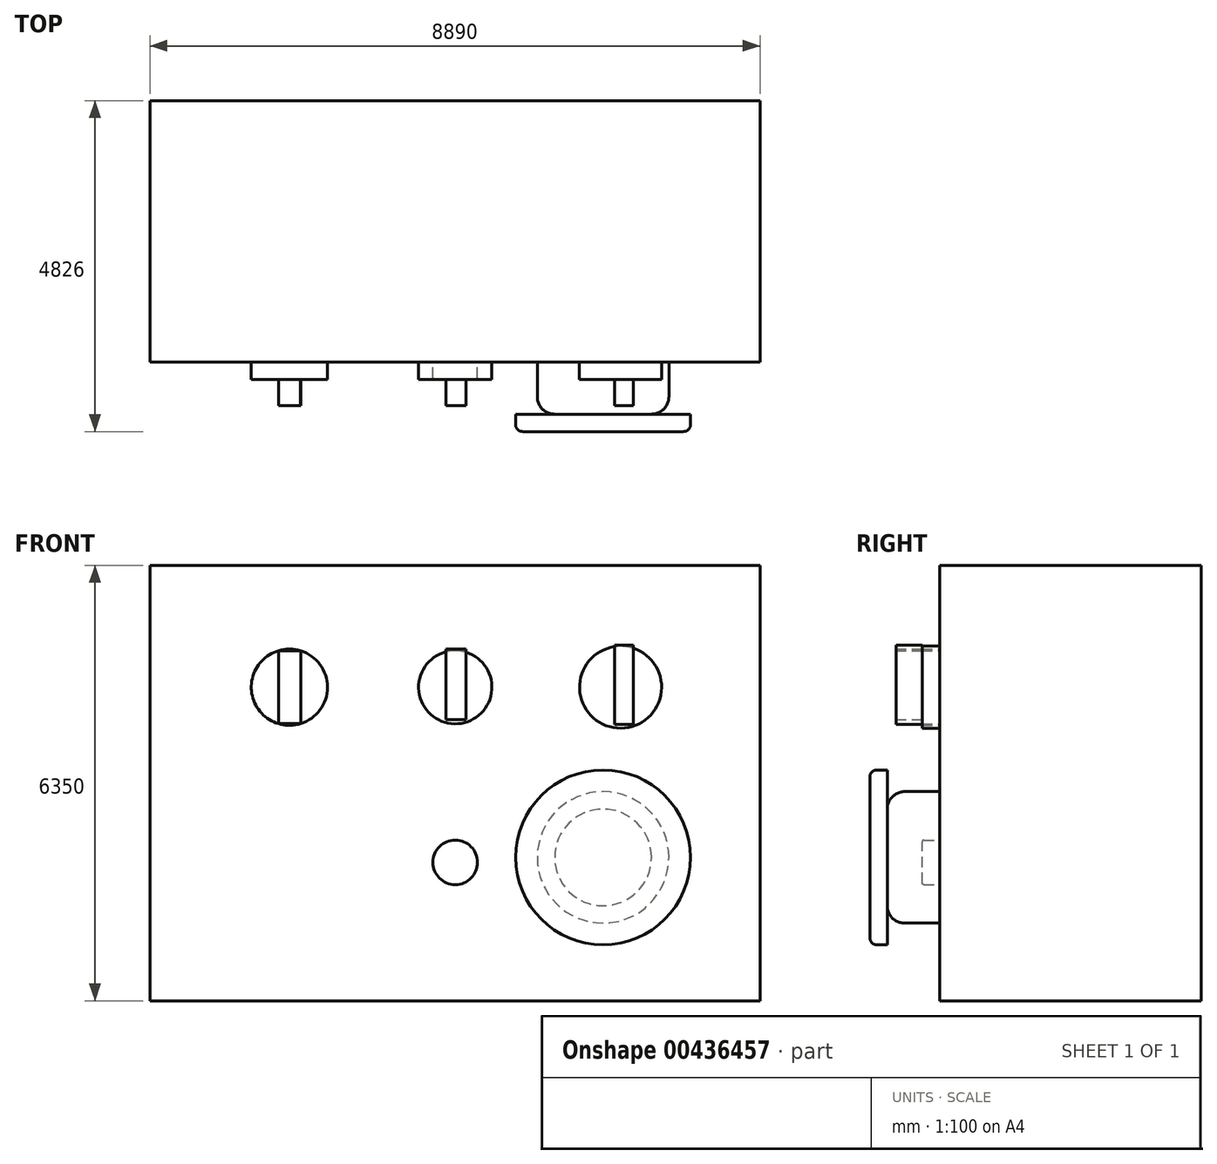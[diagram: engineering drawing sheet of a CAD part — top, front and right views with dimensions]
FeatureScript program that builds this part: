
annotation { "Feature Type Name" : "Feature", "Feature Type Description" : "" }
export const myFeature = defineFeature(function(context is Context, id is Id, definition is map)
    precondition{}
    {
        {
            var Q0;
            Q0=qCreatedBy(makeId("Front.planeOp"),FACE);
            var sketch = newSketch(context, id + "F0", { "sketchPlane" : qUnion([Q0])});
            skLineSegment(sketch, "E0.bottom", {"start": v(-4449.16, 3553.43) * mm, "end": v(4440.84, 3553.43) * mm});
            skLineSegment(sketch, "E0.top", {"start": v(-4449.16, -2796.57) * mm, "end": v(4440.84, -2796.57) * mm});
            skLineSegment(sketch, "E0.left", {"start": v(-4449.16, 3553.43) * mm, "end": v(-4449.16, -2796.57) * mm});
            skLineSegment(sketch, "E0.right", {"start": v(4440.84, 3553.43) * mm, "end": v(4440.84, -2796.57) * mm});
            skSolve(sketch);
        }
        {
            var Q0;
            Q0 = qSketchRegion(id + "F0", true);
            extrude(context, id + "F1", {"entities" : qUnion([Q0]), "depth" : 3810 * mm});
        }
        {
            var Q0;
            Q0=makeQuery(id+"F1.opExtrude","CAP_FACE",FACE,{"disambiguationData":[OSD([sQuery(id+"F0.wireOp",EDGE,"E0.bottom"),sQuery(id+"F0.wireOp",EDGE,"E0.top"),sQuery(id+"F0.wireOp",EDGE,"E0.left"),sQuery(id+"F0.wireOp",EDGE,"E0.right")])],"isStart":false});
            var sketch = newSketch(context, id + "F2", { "sketchPlane" : qUnion([Q0])});
            skCircle(sketch, "E1", {"center": v(-2417.16, 1775.43) * mm, "radius": 554.97 * mm});
            skCircle(sketch, "E2", {"center": v(0, 1775.43) * mm, "radius": 533.86 * mm});
            skCircle(sketch, "E3", {"center": v(2408.84, 1775.43) * mm, "radius": 598.02 * mm});
            skSolve(sketch);
        }
        {
            var Q0;
            Q0=makeQuery(id+"F2.imprint","IMPRINT",FACE,{"disambiguationData":[TD([[makeQuery(id+"F2.imprint","IMPRINT",EDGE,{"derivedFrom":sQuery(id+"F2.wireOp",EDGE,"E1")}),1.0]])]});
            var Q1;
            Q1=makeQuery(id+"F2.imprint","IMPRINT",FACE,{"disambiguationData":[TD([[makeQuery(id+"F2.imprint","IMPRINT",EDGE,{"derivedFrom":sQuery(id+"F2.wireOp",EDGE,"E2")}),1.0]])]});
            var Q2;
            Q2=makeQuery(id+"F2.imprint","IMPRINT",FACE,{"disambiguationData":[TD([[makeQuery(id+"F2.imprint","IMPRINT",EDGE,{"derivedFrom":sQuery(id+"F2.wireOp",EDGE,"E3")}),1.0]])]});
            extrude(context, id + "F3", {"entities" : qUnion([Q0, Q1, Q2]), "operationType" : NewBodyOperationType.ADD, "depth" : 254 * mm});
        }
        {
            var Q0;
            Q0=makeQuery(id+"F3.opExtrude","CAP_FACE",FACE,{"disambiguationData":[OSD([sQuery(id+"F2.wireOp",EDGE,"E1")])],"isStart":false});
            var sketch = newSketch(context, id + "F4", { "sketchPlane" : qUnion([Q0])});
            skLineSegment(sketch, "E4.bottom", {"start": v(-2575.27, 2307.4) * mm, "end": v(-2253, 2307.4) * mm});
            skLineSegment(sketch, "E4.top", {"start": v(-2575.27, 1245.3) * mm, "end": v(-2253, 1245.3) * mm});
            skLineSegment(sketch, "E4.left", {"start": v(-2575.27, 2307.4) * mm, "end": v(-2575.27, 1245.3) * mm});
            skLineSegment(sketch, "E4.right", {"start": v(-2253, 2307.4) * mm, "end": v(-2253, 1245.3) * mm});
            skLineSegment(sketch, "E5.bottom", {"start": v(-135.55, 2328.87) * mm, "end": v(154.96, 2328.87) * mm});
            skLineSegment(sketch, "E5.top", {"start": v(-135.55, 1303.72) * mm, "end": v(154.96, 1303.72) * mm});
            skLineSegment(sketch, "E5.left", {"start": v(-135.55, 2328.87) * mm, "end": v(-135.55, 1303.72) * mm});
            skLineSegment(sketch, "E5.right", {"start": v(154.96, 2328.87) * mm, "end": v(154.96, 1303.72) * mm});
            skLineSegment(sketch, "E6.bottom", {"start": v(2320.28, 2388.38) * mm, "end": v(2593.52, 2388.38) * mm});
            skLineSegment(sketch, "E6.top", {"start": v(2320.28, 1231.47) * mm, "end": v(2593.52, 1231.47) * mm});
            skLineSegment(sketch, "E6.left", {"start": v(2320.28, 2388.38) * mm, "end": v(2320.28, 1231.47) * mm});
            skLineSegment(sketch, "E6.right", {"start": v(2593.52, 2388.38) * mm, "end": v(2593.52, 1231.47) * mm});
            skSolve(sketch);
        }
        {
            var Q0;
            {var subQ1=sQuery(id+"F4.wireOp",EDGE,"E4.top");Q0=makeQuery(id+"F4.imprint","IMPRINT",FACE,{"disambiguationData":[TD([[makeQuery(id+"F4.imprint","IMPRINT",EDGE,{"derivedFrom":subQ1}),1.0]])]});}
            var Q1;
            Q1=makeQuery(id+"F4.imprint","IMPRINT",FACE,{"disambiguationData":[TD([[makeQuery(id+"F4.imprint","IMPRINT",EDGE,{"derivedFrom":sQuery(id+"F4.wireOp",EDGE,"E5.bottom")}),-1.0]])]});
            var Q2;
            Q2=makeQuery(id+"F4.imprint","IMPRINT",FACE,{"disambiguationData":[TD([[makeQuery(id+"F4.imprint","IMPRINT",EDGE,{"derivedFrom":sQuery(id+"F4.wireOp",EDGE,"E6.bottom")}),-1.0]])]});
            extrude(context, id + "F5", {"entities" : qUnion([Q0, Q1, Q2]), "operationType" : NewBodyOperationType.ADD, "depth" : 381 * mm});
        }
        {
            var Q0;
            Q0=makeQuery(id+"F1.opExtrude","CAP_FACE",FACE,{"disambiguationData":[OSD([sQuery(id+"F0.wireOp",EDGE,"E0.bottom"),sQuery(id+"F0.wireOp",EDGE,"E0.top"),sQuery(id+"F0.wireOp",EDGE,"E0.left"),sQuery(id+"F0.wireOp",EDGE,"E0.right")])],"isStart":false});
            var sketch = newSketch(context, id + "F6", { "sketchPlane" : qUnion([Q0])});
            skCircle(sketch, "E7", {"center": v(0, -778.37) * mm, "radius": 324.74 * mm});
            skSolve(sketch);
        }
        {
            var Q0;
            Q0=makeQuery(id+"F6.imprint","IMPRINT",FACE,{"disambiguationData":[TD([[makeQuery(id+"F6.imprint","IMPRINT",EDGE,{"derivedFrom":sQuery(id+"F6.wireOp",EDGE,"E7")}),1.0]])]});
            extrude(context, id + "F7", {"entities" : qUnion([Q0]), "operationType" : NewBodyOperationType.ADD, "depth" : 254 * mm});
        }
        {
            var Q0;
            Q0=makeQuery(id+"F7.opExtrude","CAP_EDGE",EDGE,{"disambiguationData":[OSD([sQuery(id+"F6.wireOp",EDGE,"E7")])],"isStart":false});
            fillet(context, id + "F8", {"entities" : qUnion([Q0]), "radius" : 25.4 * mm, "tangentPropagation" : true, "allowEdgeOverflow" : false});
        }
        {
            var Q0;
            Q0=makeQuery(id+"F1.opExtrude","CAP_FACE",FACE,{"disambiguationData":[OSD([sQuery(id+"F0.wireOp",EDGE,"E0.bottom"),sQuery(id+"F0.wireOp",EDGE,"E0.top"),sQuery(id+"F0.wireOp",EDGE,"E0.left"),sQuery(id+"F0.wireOp",EDGE,"E0.right")])],"isStart":false});
            var sketch = newSketch(context, id + "F9", { "sketchPlane" : qUnion([Q0])});
            skCircle(sketch, "E8", {"center": v(2154, -705.8) * mm, "radius": 958.7 * mm});
            skSolve(sketch);
        }
        {
            var Q0;
            Q0=makeQuery(id+"F9.imprint","IMPRINT",FACE,{"disambiguationData":[TD([[makeQuery(id+"F9.imprint","IMPRINT",EDGE,{"derivedFrom":sQuery(id+"F9.wireOp",EDGE,"E8")}),1.0]])]});
            extrude(context, id + "F10", {"entities" : qUnion([Q0]), "operationType" : NewBodyOperationType.ADD, "depth" : 762 * mm});
        }
        {
            var Q0;
            Q0=makeQuery(id+"F10.opExtrude","CAP_EDGE",EDGE,{"disambiguationData":[OSD([sQuery(id+"F9.wireOp",EDGE,"E8")])],"isStart":false});
            fillet(context, id + "F11", {"entities" : qUnion([Q0]), "radius" : 254 * mm, "tangentPropagation" : true, "allowEdgeOverflow" : false});
        }
        {
            var Q0;
            Q0=makeQuery(id+"F10.opExtrude","CAP_FACE",FACE,{"disambiguationData":[OSD([sQuery(id+"F9.wireOp",EDGE,"E8")])],"isStart":false});
            var sketch = newSketch(context, id + "F12", { "sketchPlane" : qUnion([Q0])});
            skCircle(sketch, "E9", {"center": v(2154, -705.8) * mm, "radius": 1274.23 * mm});
            skSolve(sketch);
        }
        {
            var Q0;
            Q0 = qSketchRegion(id + "F12", true);
            extrude(context, id + "F13", {"entities" : qUnion([Q0]), "operationType" : NewBodyOperationType.ADD, "depth" : 254 * mm});
        }
        {
            var Q0;
            Q0=makeQuery(id+"F13.opExtrude","CAP_EDGE",EDGE,{"disambiguationData":[OSD([sQuery(id+"F12.wireOp",EDGE,"E9")])],"isStart":false});
            fillet(context, id + "F14", {"entities" : qUnion([Q0]), "radius" : 101.6 * mm, "tangentPropagation" : true, "allowEdgeOverflow" : false});
        }
    });
